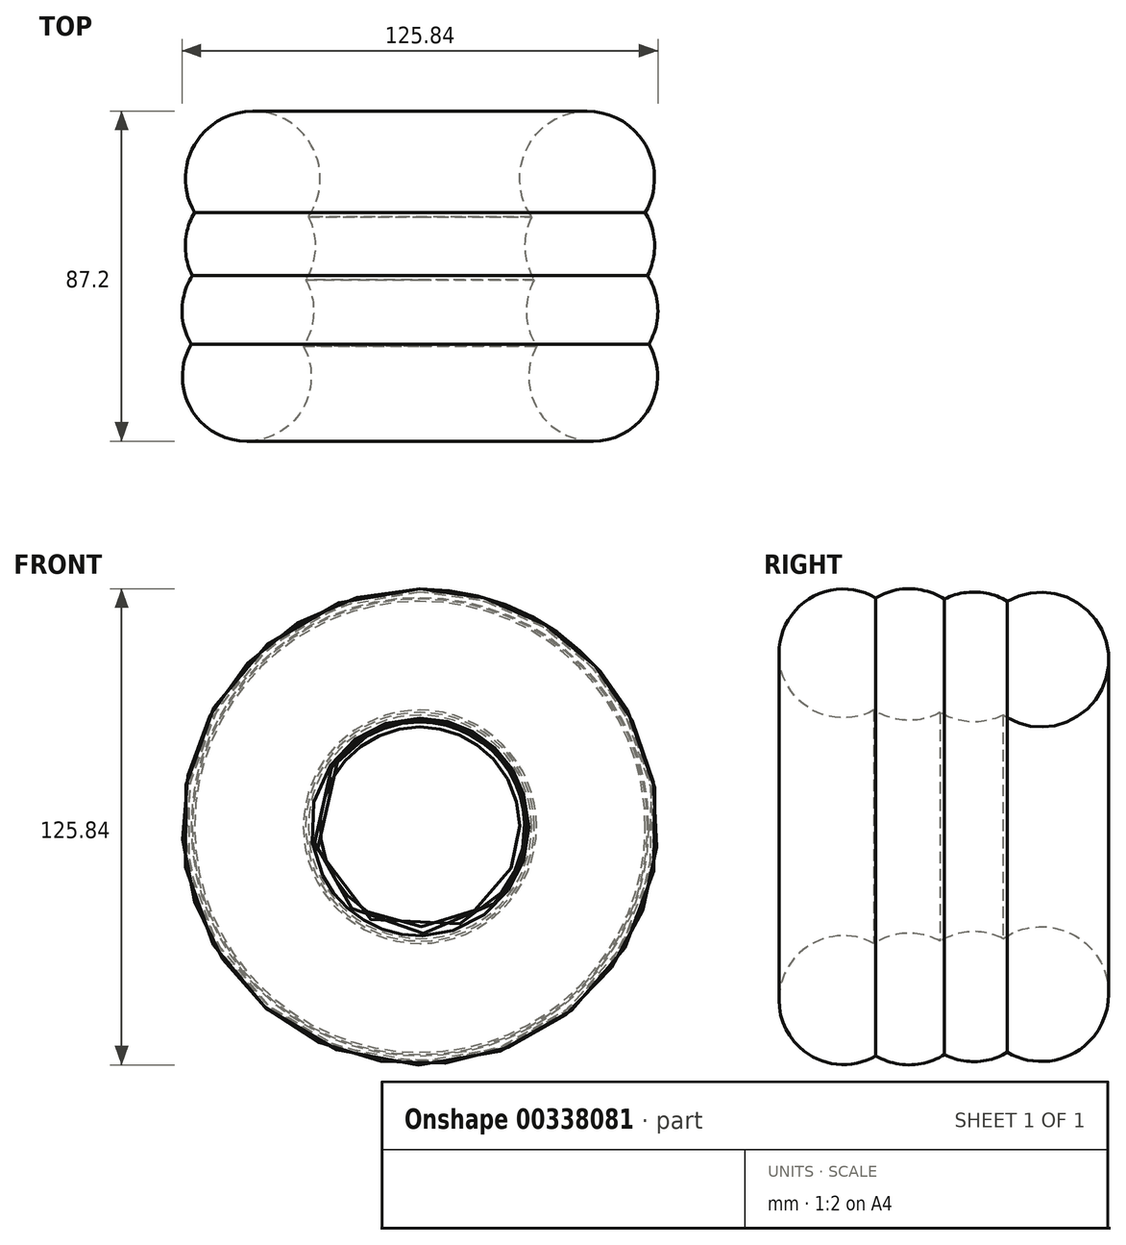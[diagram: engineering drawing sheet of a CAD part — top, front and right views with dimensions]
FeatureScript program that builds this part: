
annotation { "Feature Type Name" : "Feature", "Feature Type Description" : "" }
export const myFeature = defineFeature(function(context is Context, id is Id, definition is map)
    precondition{}
    {
        {
            var Q0;
            Q0=qCreatedBy(makeId("Top.planeOp"),FACE);
            var sketch = newSketch(context, id + "F0", { "sketchPlane" : qUnion([Q0])});
            skArc(sketch, "E0", {"start": v(-29.53, 18.6) * mm, "mid": v(-43.52, 46.52) * mm, "end": v(-59.6, 19.75) * mm});
            skArc(sketch, "E1", {"start": v(-30.2, 1.99) * mm, "mid": v(-27.72, 10.2) * mm, "end": v(-29.53, 18.6) * mm});
            skArc(sketch, "E2", {"start": v(-30.82, -15.54) * mm, "mid": v(-28.14, -6.86) * mm, "end": v(-30.2, 1.99) * mm});
            skArc(sketch, "E3", {"start": v(-60.51, -15.07) * mm, "mid": v(-46.07, -40.67) * mm, "end": v(-30.82, -15.54) * mm});
            skArc(sketch, "E4.trimOffspring", {"start": v(-46.83, 11.1) * mm, "mid": v(-44.87, 10.9) * mm, "end": v(-42.9, 10.94) * mm});
            skArc(sketch, "E5.trimOffspring", {"start": v(-60.18, 3.11) * mm, "mid": v(-62.91, -5.93) * mm, "end": v(-60.51, -15.07) * mm});
            skArc(sketch, "E6.trimOffspring", {"start": v(-59.6, 19.75) * mm, "mid": v(-62.04, 11.5) * mm, "end": v(-60.18, 3.11) * mm});
            skLineSegment(sketch, "E7", {"start": v(0, 49.04) * mm, "end": v(0, -46.46) * mm});
            skSolve(sketch);
        }
        {
            var Q0;
            Q0 = qSketchRegion(id + "F0", true);
            var Q1;
            Q1=sQuery(id+"F0.wireOp",EDGE,"E7");
            revolve(context, id + "F1", {"entities" : qUnion([Q0]), "axis" : qUnion([Q1]), "revolveType" : RevolveType.FULL});
        }
    });
